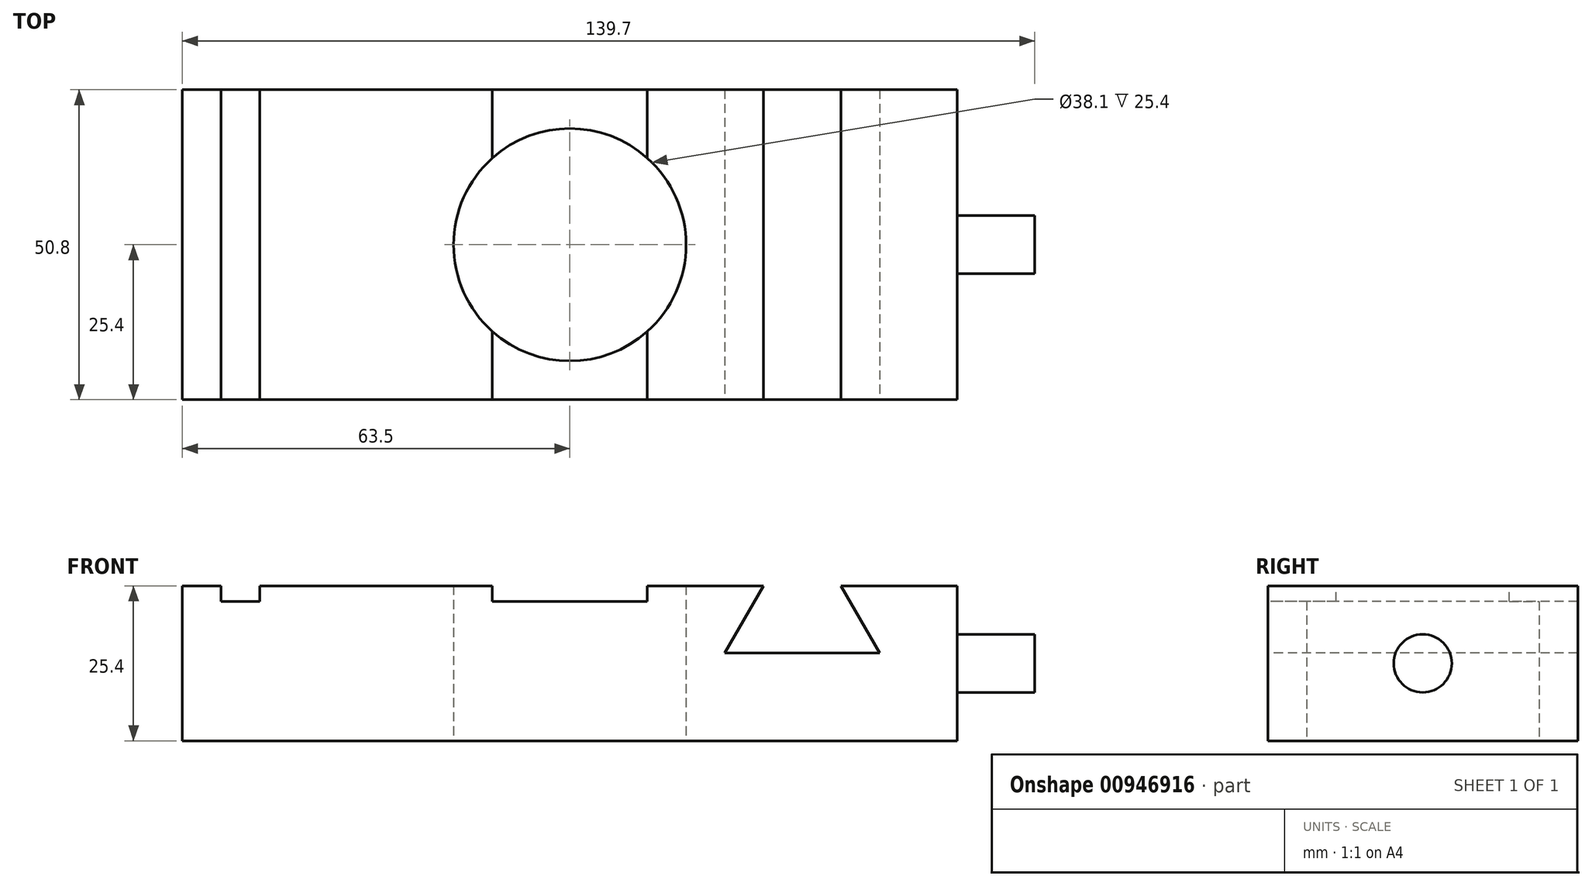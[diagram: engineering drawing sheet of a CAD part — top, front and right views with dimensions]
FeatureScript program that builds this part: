
annotation { "Feature Type Name" : "Feature", "Feature Type Description" : "" }
export const myFeature = defineFeature(function(context is Context, id is Id, definition is map)
    precondition{}
    {
        {
            var Q0;
            Q0=qCreatedBy(makeId("Top.planeOp"),FACE);
            var sketch = newSketch(context, id + "F0", { "sketchPlane" : qUnion([Q0])});
            skLineSegment(sketch, "E0.bottom", {"start": v(-63.5, 25.4) * mm, "end": v(63.5, 25.4) * mm});
            skLineSegment(sketch, "E0.top", {"start": v(-63.5, -25.4) * mm, "end": v(63.5, -25.4) * mm});
            skLineSegment(sketch, "E0.left", {"start": v(-63.5, 25.4) * mm, "end": v(-63.5, -25.4) * mm});
            skLineSegment(sketch, "E0.right", {"start": v(63.5, 25.4) * mm, "end": v(63.5, -25.4) * mm});
            skPoint(sketch, "E0.middle", {"position": v(0, 0) * mm});
            skCircle(sketch, "E1", {"center": v(0, 0) * mm, "radius": 2.55 * mm});
            skCircle(sketch, "E2", {"center": v(0, 0) * mm, "radius": 19.05 * mm});
            skSolve(sketch);
        }
        {
            var Q0;
            Q0=makeQuery(id+"F0.imprint","IMPRINT",FACE,{"disambiguationData":[TD([[makeQuery(id+"F0.imprint","IMPRINT",EDGE,{"derivedFrom":sQuery(id+"F0.wireOp",EDGE,"E0.bottom")}),-1.0]])]});
            extrude(context, id + "F1", {"entities" : qUnion([Q0]), "depth" : 25.4 * mm, "offsetDistance" : 25.4 * mm});
        }
        {
            var Q0;
            Q0=makeQuery(id+"F1.opExtrude","CAP_FACE",FACE,{"disambiguationData":[OSD([sQuery(id+"F0.wireOp",EDGE,"E0.bottom"),sQuery(id+"F0.wireOp",EDGE,"E0.top"),sQuery(id+"F0.wireOp",EDGE,"E0.left"),sQuery(id+"F0.wireOp",EDGE,"E0.right"),sQuery(id+"F0.wireOp",EDGE,"E2")])],"isStart":false});
            var sketch = newSketch(context, id + "F2", { "sketchPlane" : qUnion([Q0])});
            skLineSegment(sketch, "E3.bottom", {"start": v(-57.15, 25.4) * mm, "end": v(-50.8, 25.4) * mm});
            skLineSegment(sketch, "E3.top", {"start": v(-57.15, -25.4) * mm, "end": v(-50.8, -25.4) * mm});
            skLineSegment(sketch, "E3.left", {"start": v(-57.15, 25.4) * mm, "end": v(-57.15, -25.4) * mm});
            skLineSegment(sketch, "E3.right", {"start": v(-50.8, 25.4) * mm, "end": v(-50.8, -25.4) * mm});
            skLineSegment(sketch, "E4.bottom", {"start": v(-12.7, 25.4) * mm, "end": v(12.7, 25.4) * mm});
            skLineSegment(sketch, "E4.top", {"start": v(-12.7, -25.4) * mm, "end": v(12.7, -25.4) * mm});
            skLineSegment(sketch, "E4.left", {"start": v(12.7, 25.4) * mm, "end": v(12.7, -25.4) * mm});
            skLineSegment(sketch, "E4.right", {"start": v(-12.7, 25.4) * mm, "end": v(-12.7, -25.4) * mm});
            skPoint(sketch, "E5", {"position": v(0, 0) * mm});
            skPoint(sketch, "E6", {"position": v(0, 25.4) * mm});
            skLineSegment(sketch, "E7", {"start": v(0, 25.4) * mm, "end": v(0, -25.4) * mm, "construction": true});
            skSolve(sketch);
        }
        {
            var Q0;
            Q0=makeQuery(id+"F2.imprint","IMPRINT",FACE,{"disambiguationData":[TD([[makeQuery(id+"F2.imprint","IMPRINT",EDGE,{"derivedFrom":sQuery(id+"F2.wireOp",EDGE,"E3.bottom")}),-1.0]])]});
            var Q1;
            {var subQ0=sQuery(id+"F2.wireOp",EDGE,"E4.top");Q1=makeQuery(id+"F2.imprint","IMPRINT",FACE,{"disambiguationData":[TD([[makeQuery(id+"F2.imprint","IMPRINT",EDGE,{"derivedFrom":subQ0}),1.0]])]});}
            var Q2;
            {var subQ0=sQuery(id+"F2.wireOp",EDGE,"E4.bottom");Q2=makeQuery(id+"F2.imprint","IMPRINT",FACE,{"disambiguationData":[TD([[makeQuery(id+"F2.imprint","IMPRINT",EDGE,{"derivedFrom":subQ0}),-1.0]])]});}
            extrude(context, id + "F3", {"entities" : qUnion([Q0, Q1, Q2]), "operationType" : NewBodyOperationType.REMOVE, "oppositeDirection" : true, "depth" : 2.54 * mm, "offsetDistance" : 25.4 * mm});
        }
        {
            var Q0;
            Q0=makeQuery(id+"F1.opExtrude","SWEPT_FACE",FACE,{"disambiguationData":[OSD([sQuery(id+"F0.wireOp",EDGE,"E0.top")])]});
            var sketch = newSketch(context, id + "F4", { "sketchPlane" : qUnion([Q0])});
            skLineSegment(sketch, "E8", {"start": v(31.75, 25.4) * mm, "end": v(25.4, 14.4) * mm});
            skLineSegment(sketch, "E9", {"start": v(25.4, 14.4) * mm, "end": v(50.8, 14.4) * mm});
            skLineSegment(sketch, "E10", {"start": v(50.8, 14.4) * mm, "end": v(44.45, 25.4) * mm});
            skLineSegment(sketch, "E11", {"start": v(44.45, 25.4) * mm, "end": v(31.75, 25.4) * mm});
            skPoint(sketch, "E12", {"position": v(44.45, 25.4) * mm});
            skLineSegment(sketch, "E13", {"start": v(31.75, 25.4) * mm, "end": v(44.45, 25.4) * mm});
            skPoint(sketch, "E14", {"position": v(38.1, 25.4) * mm});
            skSolve(sketch);
        }
        {
            var Q0;
            Q0=makeQuery(id+"F4.imprint","IMPRINT",FACE,{"disambiguationData":[TD([[makeQuery(id+"F4.imprint","IMPRINT",EDGE,{"derivedFrom":sQuery(id+"F4.wireOp",EDGE,"E8")}),1.0]])]});
            extrude(context, id + "F5", {"entities" : qUnion([Q0]), "operationType" : NewBodyOperationType.REMOVE, "oppositeDirection" : true, "depth" : 67.56 * mm, "offsetDistance" : 25.4 * mm});
        }
        {
            var Q0;
            Q0=makeQuery(id+"F1.opExtrude","SWEPT_FACE",FACE,{"disambiguationData":[OSD([sQuery(id+"F0.wireOp",EDGE,"E0.right")])]});
            var sketch = newSketch(context, id + "F6", { "sketchPlane" : qUnion([Q0])});
            skPoint(sketch, "E15.centerSnap0", {"position": v(0, 25.4) * mm});
            skPoint(sketch, "E15.centerSnap1", {"position": v(-25.4, 12.7) * mm});
            skCircle(sketch, "E16", {"center": v(0, 12.7) * mm, "radius": 4.76 * mm});
            skSolve(sketch);
        }
        {
            var Q0;
            Q0=makeQuery(id+"F6.imprint","IMPRINT",FACE,{"disambiguationData":[TD([[makeQuery(id+"F6.imprint","IMPRINT",EDGE,{"derivedFrom":sQuery(id+"F6.wireOp",EDGE,"E16")}),1.0]])]});
            extrude(context, id + "F7", {"entities" : qUnion([Q0]), "operationType" : NewBodyOperationType.ADD, "depth" : 12.7 * mm, "offsetDistance" : 25.4 * mm});
        }
    });
